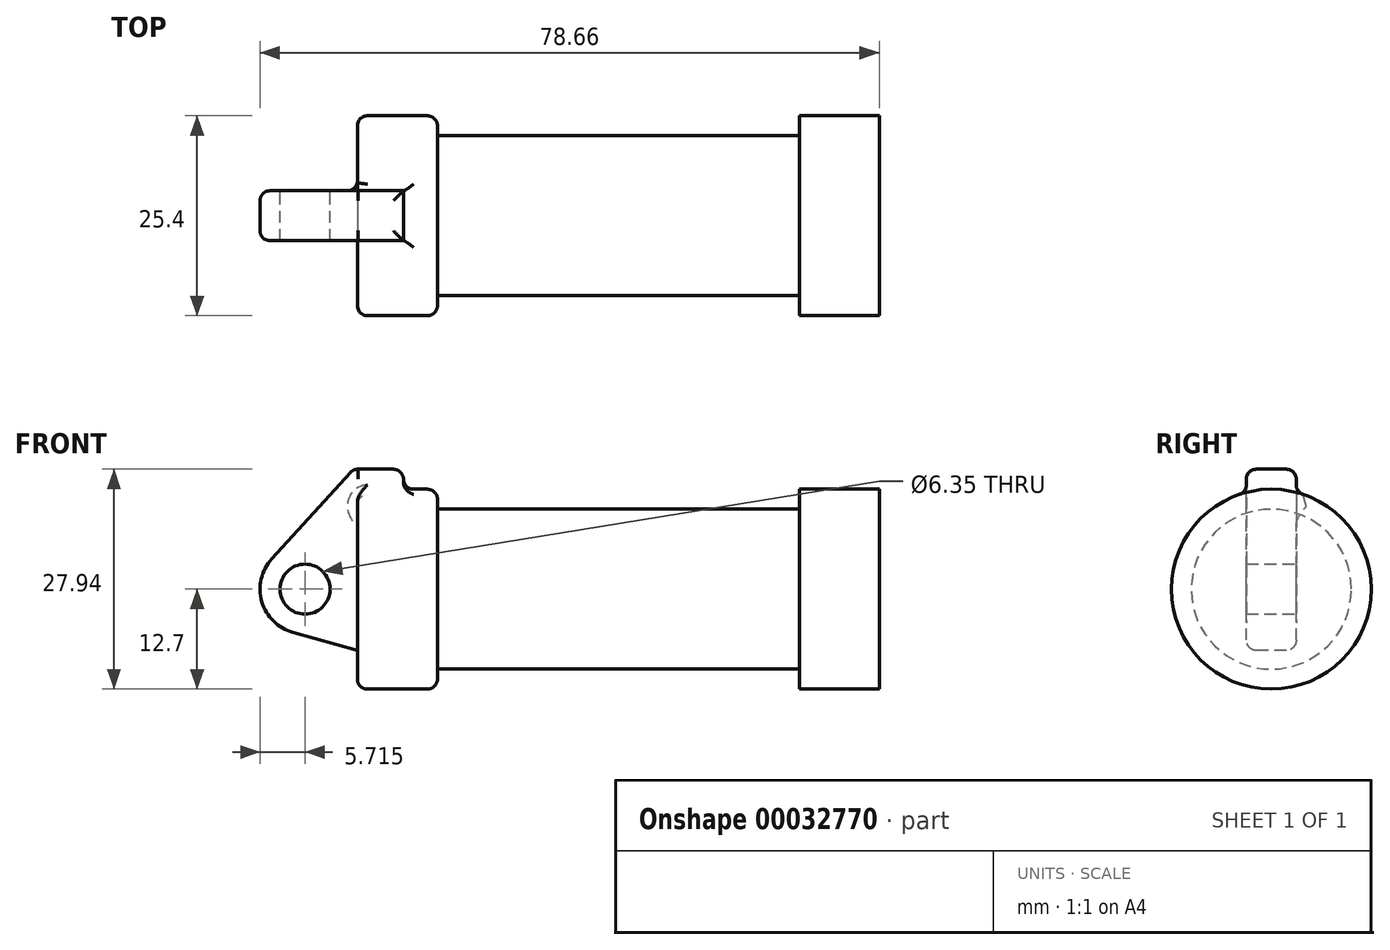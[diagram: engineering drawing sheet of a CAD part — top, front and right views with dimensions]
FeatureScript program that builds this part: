
annotation { "Feature Type Name" : "Feature", "Feature Type Description" : "" }
export const myFeature = defineFeature(function(context is Context, id is Id, definition is map)
    precondition{}
    {
        {
            var Q0;
            Q0=qCreatedBy(makeId("Front.planeOp"),FACE);
            var sketch = newSketch(context, id + "F0", { "sketchPlane" : qUnion([Q0])});
            skLineSegment(sketch, "E0", {"start": v(10.16, 12.7) * mm, "end": v(10.16, 10.16) * mm});
            skLineSegment(sketch, "E1", {"start": v(10.16, 10.16) * mm, "end": v(56.13, 10.16) * mm});
            skLineSegment(sketch, "E2", {"start": v(56.13, 10.16) * mm, "end": v(56.13, 12.7) * mm});
            skLineSegment(sketch, "E3", {"start": v(56.13, 12.7) * mm, "end": v(66.3, 12.7) * mm});
            skLineSegment(sketch, "E4", {"start": v(66.3, 12.7) * mm, "end": v(66.3, 0) * mm});
            skLineSegment(sketch, "E5", {"start": v(66.3, 0) * mm, "end": v(0, 0) * mm});
            skLineSegment(sketch, "E6", {"start": v(5.84, 15.24) * mm, "end": v(-0.5, 15.24) * mm});
            skLineSegment(sketch, "E7", {"start": v(-0.5, 15.24) * mm, "end": v(-10.88, 3.85) * mm});
            skLineSegment(sketch, "E8", {"start": v(0, 0) * mm, "end": v(-6.65, 0) * mm});
            skCircle(sketch, "E9", {"center": v(-6.65, 0) * mm, "radius": 5.72 * mm});
            skCircle(sketch, "E10", {"center": v(-6.65, 0) * mm, "radius": 3.18 * mm});
            skLineSegment(sketch, "E11", {"start": v(5.84, 15.24) * mm, "end": v(5.84, -9.4) * mm});
            skLineSegment(sketch, "E12", {"start": v(5.84, -9.4) * mm, "end": v(-8.18, -5.5) * mm});
            skLineSegment(sketch, "E13", {"start": v(10.16, 12.7) * mm, "end": v(5.84, 12.7) * mm});
            skSolve(sketch);
        }
        {
            var Q0;
            Q0=makeQuery(id+"F0.imprint","IMPRINT",FACE,{"disambiguationData":[TD([[makeQuery(id+"F0.imprint","IMPRINT",EDGE,{"derivedFrom":sQuery(id+"F0.wireOp",EDGE,"E0")}),-1.0]])]});
            var Q1;
            Q1=sQuery(id+"F0.wireOp",EDGE,"E5");
            revolve(context, id + "F1", {"entities" : qUnion([Q0]), "axis" : qUnion([Q1]), "revolveType" : RevolveType.FULL});
        }
        {
            var Q0;
            Q0=makeQuery(id+"F1.opRevolve","SWEPT_FACE",FACE,{"disambiguationData":[OSD([sQuery(id+"F0.wireOp",EDGE,"E11")])]});
            extrude(context, id + "F2", {"entities" : qUnion([Q0]), "operationType" : NewBodyOperationType.ADD, "depth" : 5.84 * mm});
        }
        {
            var Q0;
            {var subQ0=sQuery(id+"F0.wireOp",EDGE,"E12");Q0=makeQuery(id+"F0.imprint","IMPRINT",FACE,{"disambiguationData":[TD([[makeQuery(id+"F0.imprint","IMPRINT",EDGE,{"derivedFrom":subQ0}),-1.0]])]});}
            var Q1;
            {var subQ8=sQuery(id+"F0.wireOp",EDGE,"E6");Q1=makeQuery(id+"F0.imprint","IMPRINT",FACE,{"disambiguationData":[TD([[makeQuery(id+"F0.imprint","IMPRINT",EDGE,{"derivedFrom":subQ8}),1.0]])]});}
            var Q2;
            {var subQ0=sQuery(id+"F0.wireOp",EDGE,"E10");Q2=makeQuery(id+"F0.imprint","IMPRINT",FACE,{"disambiguationData":[TD([[makeQuery(id+"F0.imprint","IMPRINT",EDGE,{"derivedFrom":subQ0}),-1.0]])]});}
            extrude(context, id + "F3", {"entities" : qUnion([Q0, Q1, Q2]), "operationType" : NewBodyOperationType.ADD, "depth" : 3.17 * mm, "hasSecondDirection" : true, "secondDirectionOppositeDirection" : true, "secondDirectionDepth" : 3.17 * mm});
        }
        {
            var Q0;
            Q0=makeQuery(id+"F3.opExtrude","CAP_EDGE",EDGE,{"disambiguationData":[OSD([sQuery(id+"F0.wireOp",EDGE,"E6")])],"isStart":false});
            var Q1;
            {var subQ0=sQuery(id+"F0.wireOp",EDGE,"E13");var subQ1=sQuery(id+"F0.wireOp",EDGE,"E11");Q1=makeQuery(id+"F3.boolean.opBoolean","INTERSECT",EDGE,{"derivedFrom":[makeQuery(id+"F2.boolean.opBoolean","MERGE",FACE,{"derivedFrom":[makeQuery(id+"F1.opRevolve","SWEPT_FACE",FACE,{"disambiguationData":[OSD([subQ0])]}),makeQuery(id+"F2.opExtrude","SWEPT_FACE",FACE,{"disambiguationData":[OSD([subQ1,subQ0])]})]}),makeQuery(id+"F3.opExtrude","CAP_FACE",FACE,{"disambiguationData":[OSD([sQuery(id+"F0.wireOp",EDGE,"E6"),sQuery(id+"F0.wireOp",EDGE,"E7"),sQuery(id+"F0.wireOp",EDGE,"E9"),sQuery(id+"F0.wireOp",EDGE,"E10"),subQ1,sQuery(id+"F0.wireOp",EDGE,"E12")])],"isStart":false})]});}
            var Q2;
            Q2=makeQuery(id+"F3.opExtrude","SWEPT_EDGE",EDGE,{"disambiguationData":[OSD([sQuery(id+"F0.wireOp",EDGE,"E6"),sQuery(id+"F0.wireOp",EDGE,"E11")])]});
            var Q3;
            Q3=makeQuery(id+"F3.opExtrude","CAP_EDGE",EDGE,{"disambiguationData":[OSD([sQuery(id+"F0.wireOp",EDGE,"E6")])],"isStart":true});
            fillet(context, id + "F4", {"entities" : qUnion([Q0, Q1, Q2, Q3]), "radius" : 1.27 * mm, "tangentPropagation" : true, "allowEdgeOverflow" : false});
        }
        {
            var Q0;
            Q0=makeQuery(id+"F3.opExtrude","CAP_EDGE",EDGE,{"disambiguationData":[OSD([sQuery(id+"F0.wireOp",EDGE,"E7")])],"isStart":false});
            fillet(context, id + "F5", {"entities" : qUnion([Q0]), "radius" : 1.27 * mm, "tangentPropagation" : true, "allowEdgeOverflow" : false});
        }
        {
            var Q0;
            {var subQ0=sQuery(id+"F0.wireOp",EDGE,"E13");Q0=makeQuery(id+"F2.boolean.opBoolean","MERGE",FACE,{"derivedFrom":[makeQuery(id+"F1.opRevolve","SWEPT_FACE",FACE,{"disambiguationData":[OSD([subQ0])]}),makeQuery(id+"F2.opExtrude","SWEPT_FACE",FACE,{"disambiguationData":[OSD([sQuery(id+"F0.wireOp",EDGE,"E11"),subQ0])]})]});}
            fillet(context, id + "F6", {"entities" : qUnion([Q0]), "radius" : 1.27 * mm, "tangentPropagation" : true, "allowEdgeOverflow" : false});
        }
    });
